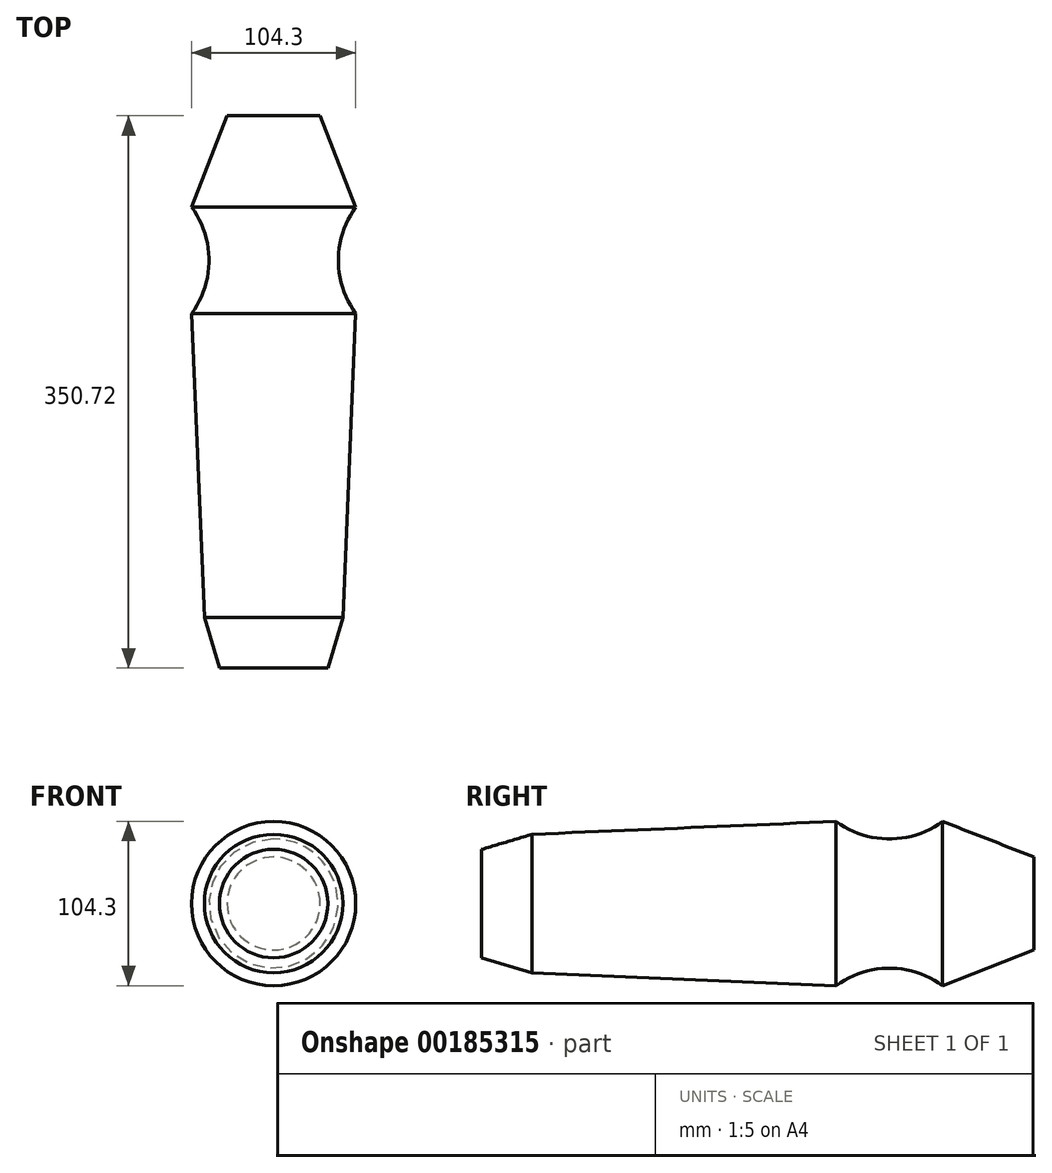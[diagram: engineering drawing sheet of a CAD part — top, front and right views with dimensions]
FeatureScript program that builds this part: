
annotation { "Feature Type Name" : "Feature", "Feature Type Description" : "" }
export const myFeature = defineFeature(function(context is Context, id is Id, definition is map)
    precondition{}
    {
        {
            var Q0;
            Q0=qCreatedBy(makeId("Right.planeOp"),FACE);
            var sketch = newSketch(context, id + "F0", { "sketchPlane" : qUnion([Q0])});
            skLineSegment(sketch, "E0", {"start": v(175.36, 0) * mm, "end": v(-175.36, 0) * mm});
            skLineSegment(sketch, "E1", {"start": v(-175.36, 0) * mm, "end": v(-175.36, 34.44) * mm});
            skLineSegment(sketch, "E2", {"start": v(-143.32, 0) * mm, "end": v(-143.32, 43.98) * mm, "construction": true});
            skLineSegment(sketch, "E3", {"start": v(49.76, 0) * mm, "end": v(49.76, 52.15) * mm, "construction": true});
            skLineSegment(sketch, "E4", {"start": v(83.56, 0) * mm, "end": v(83.56, 41.05) * mm, "construction": true});
            skLineSegment(sketch, "E5", {"start": v(117.37, 0) * mm, "end": v(117.37, 52.15) * mm, "construction": true});
            skLineSegment(sketch, "E6", {"start": v(175.36, 0) * mm, "end": v(175.36, 29.53) * mm});
            skLineSegment(sketch, "E7", {"start": v(175.36, 29.53) * mm, "end": v(117.37, 52.15) * mm});
            skArc(sketch, "E8", {"start": v(49.76, 52.15) * mm, "mid": v(83.56, 41.05) * mm, "end": v(117.37, 52.15) * mm});
            skLineSegment(sketch, "E9", {"start": v(-143.32, 43.98) * mm, "end": v(49.76, 52.15) * mm});
            skLineSegment(sketch, "E10", {"start": v(-175.36, 34.44) * mm, "end": v(-143.32, 43.98) * mm});
            skSolve(sketch);
        }
        {
            var Q0;
            Q0=makeQuery(id+"F0.imprint","IMPRINT",FACE,{"disambiguationData":[TD([[makeQuery(id+"F0.imprint","IMPRINT",EDGE,{"derivedFrom":sQuery(id+"F0.wireOp",EDGE,"E0")}),-1.0]])]});
            var Q1;
            Q1=sQuery(id+"F0.wireOp",EDGE,"E0");
            revolve(context, id + "F1", {"entities" : qUnion([Q0]), "axis" : qUnion([Q1]), "revolveType" : RevolveType.FULL});
        }
    });
